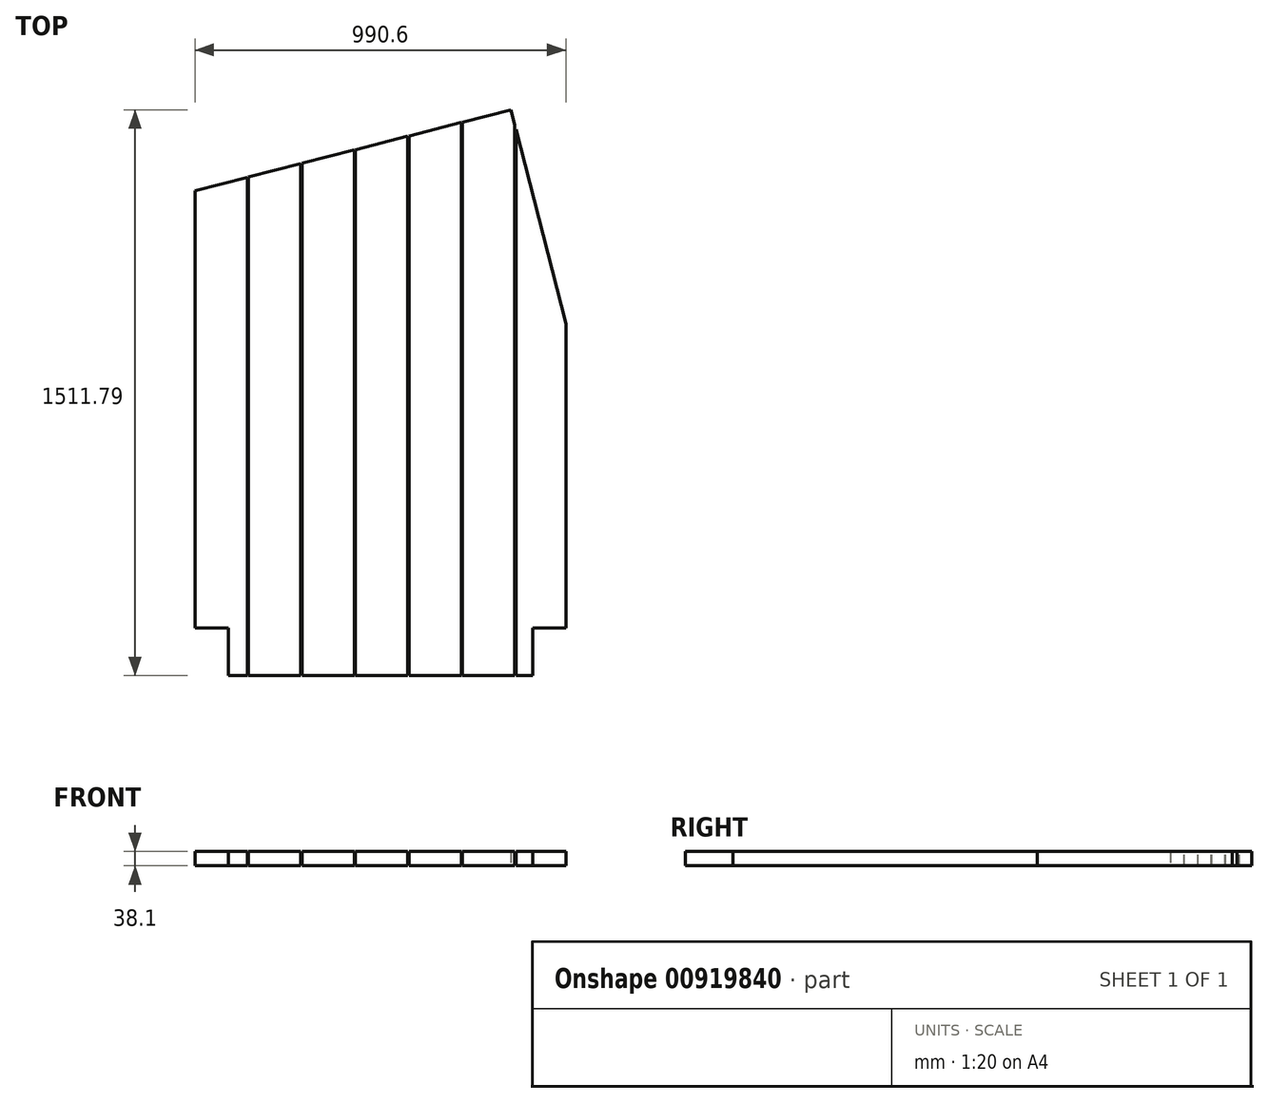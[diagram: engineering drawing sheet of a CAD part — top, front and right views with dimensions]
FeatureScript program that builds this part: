
annotation { "Feature Type Name" : "Feature", "Feature Type Description" : "" }
export const myFeature = defineFeature(function(context is Context, id is Id, definition is map)
    precondition{}
    {
        {
            var Q0;
            Q0=qCreatedBy(makeId("Top.planeOp"),FACE);
            var sketch = newSketch(context, id + "F0", { "sketchPlane" : qUnion([Q0])});
            skLineSegment(sketch, "E0", {"start": v(0, 0) * mm, "end": v(0, 1168.4) * mm});
            skLineSegment(sketch, "E1", {"start": v(0, 1168.4) * mm, "end": v(843.93, 1384.8) * mm});
            skLineSegment(sketch, "E2", {"start": v(843.93, 1384.8) * mm, "end": v(990.6, 812.8) * mm});
            skLineSegment(sketch, "E3", {"start": v(990.6, 812.8) * mm, "end": v(990.6, 0) * mm});
            skLineSegment(sketch, "E4", {"start": v(990.6, 0) * mm, "end": v(0, 0) * mm});
            skSolve(sketch);
        }
        {
            var Q0;
            Q0 = qSketchRegion(id + "F0", true);
            extrude(context, id + "F1", {"entities" : qUnion([Q0]), "depth" : 38.1 * mm, "offsetDistance" : 25.4 * mm});
        }
        {
            var Q0;
            Q0=makeQuery(id+"F1.opExtrude","CAP_FACE",FACE,{"disambiguationData":[OSD([sQuery(id+"F0.wireOp",EDGE,"E0"),sQuery(id+"F0.wireOp",EDGE,"E1"),sQuery(id+"F0.wireOp",EDGE,"E2"),sQuery(id+"F0.wireOp",EDGE,"E3"),sQuery(id+"F0.wireOp",EDGE,"E4")])],"isStart":false});
            var sketch = newSketch(context, id + "F2", { "sketchPlane" : qUnion([Q0])});
            skLineSegment(sketch, "E5.bottom", {"start": v(88.9, 0) * mm, "end": v(901.7, 0) * mm});
            skLineSegment(sketch, "E5.top", {"start": v(88.9, -127) * mm, "end": v(901.7, -127) * mm});
            skLineSegment(sketch, "E5.left", {"start": v(88.9, 0) * mm, "end": v(88.9, -127) * mm});
            skLineSegment(sketch, "E5.right", {"start": v(901.7, 0) * mm, "end": v(901.7, -127) * mm});
            skSolve(sketch);
        }
        {
            var Q0;
            Q0=makeQuery(id+"F2.imprint","IMPRINT",FACE,{"disambiguationData":[TD([[makeQuery(id+"F2.imprint","IMPRINT",EDGE,{"derivedFrom":sQuery(id+"F2.wireOp",EDGE,"E5.bottom")}),1.0]])]});
            extrude(context, id + "F3", {"entities" : qUnion([Q0]), "operationType" : NewBodyOperationType.ADD, "oppositeDirection" : true, "depth" : 38.1 * mm, "offsetDistance" : 25.4 * mm});
        }
        {
            var Q0;
            Q0=makeQuery(id+"F3.boolean.opBoolean","MERGE",FACE,{"derivedFrom":[makeQuery(id+"F1.opExtrude","CAP_FACE",FACE,{"disambiguationData":[OSD([sQuery(id+"F0.wireOp",EDGE,"E0"),sQuery(id+"F0.wireOp",EDGE,"E1"),sQuery(id+"F0.wireOp",EDGE,"E2"),sQuery(id+"F0.wireOp",EDGE,"E3"),sQuery(id+"F0.wireOp",EDGE,"E4")])],"isStart":false}),makeQuery(id+"F3.opExtrude","CAP_FACE",FACE,{"disambiguationData":[OSD([sQuery(id+"F2.wireOp",EDGE,"E5.bottom"),sQuery(id+"F2.wireOp",EDGE,"E5.top"),sQuery(id+"F2.wireOp",EDGE,"E5.left"),sQuery(id+"F2.wireOp",EDGE,"E5.right")])],"isStart":true})]});
            var sketch = newSketch(context, id + "F4", { "sketchPlane" : qUnion([Q0])});
            skLineSegment(sketch, "E6", {"start": v(139.7, -127) * mm, "end": v(139.7, 1204.22) * mm});
            skLineSegment(sketch, "E7", {"start": v(142.87, 1205.03) * mm, "end": v(142.88, -127) * mm});
            skLineSegment(sketch, "E8", {"start": v(282.57, 1240.86) * mm, "end": v(282.58, -127) * mm});
            skLineSegment(sketch, "E9", {"start": v(285.75, 1241.67) * mm, "end": v(285.75, -127) * mm});
            skLineSegment(sketch, "E10", {"start": v(425.45, 1277.49) * mm, "end": v(425.45, -127) * mm});
            skLineSegment(sketch, "E11", {"start": v(428.62, 1278.3) * mm, "end": v(428.63, -127) * mm});
            skLineSegment(sketch, "E12", {"start": v(568.33, -127) * mm, "end": v(568.32, 1314.12) * mm});
            skLineSegment(sketch, "E13", {"start": v(571.5, 1314.94) * mm, "end": v(571.5, -127) * mm});
            skLineSegment(sketch, "E14", {"start": v(711.2, 1902.46) * mm, "end": v(711.2, -127) * mm});
            skLineSegment(sketch, "E15", {"start": v(714.37, 1351.57) * mm, "end": v(714.38, -127) * mm});
            skLineSegment(sketch, "E16", {"start": v(854.08, -127) * mm, "end": v(854.07, 1387.4) * mm});
            skLineSegment(sketch, "E17", {"start": v(857.25, 1332.87) * mm, "end": v(857.25, -127) * mm});
            skLineSegment(sketch, "E18", {"start": v(996.95, 788.03) * mm, "end": v(996.95, 0) * mm});
            skSolve(sketch);
        }
        {
            var Q0;
            {var subQ0=sQuery(id+"F4.wireOp",EDGE,"E6");Q0=makeQuery(id+"F4.imprint","IMPRINT",FACE,{"disambiguationData":[TD([[makeQuery(id+"F4.imprint","IMPRINT",EDGE,{"derivedFrom":subQ0}),-1.0]])]});}
            var Q1;
            {var subQ0=sQuery(id+"F4.wireOp",EDGE,"E8");Q1=makeQuery(id+"F4.imprint","IMPRINT",FACE,{"disambiguationData":[TD([[makeQuery(id+"F4.imprint","IMPRINT",EDGE,{"derivedFrom":subQ0}),1.0]])]});}
            var Q2;
            {var subQ0=sQuery(id+"F4.wireOp",EDGE,"E10");Q2=makeQuery(id+"F4.imprint","IMPRINT",FACE,{"disambiguationData":[TD([[makeQuery(id+"F4.imprint","IMPRINT",EDGE,{"derivedFrom":subQ0}),1.0]])]});}
            var Q3;
            {var subQ0=sQuery(id+"F4.wireOp",EDGE,"E12");Q3=makeQuery(id+"F4.imprint","IMPRINT",FACE,{"disambiguationData":[TD([[makeQuery(id+"F4.imprint","IMPRINT",EDGE,{"derivedFrom":subQ0}),-1.0]])]});}
            var Q4;
            {var subQ5=sQuery(id+"F4.wireOp",EDGE,"E15");Q4=makeQuery(id+"F4.imprint","IMPRINT",FACE,{"disambiguationData":[TD([[makeQuery(id+"F4.imprint","IMPRINT",EDGE,{"derivedFrom":subQ5}),-1.0]])]});}
            var Q5;
            {var subQ5=sQuery(id+"F4.wireOp",EDGE,"E17");Q5=makeQuery(id+"F4.imprint","IMPRINT",FACE,{"disambiguationData":[TD([[makeQuery(id+"F4.imprint","IMPRINT",EDGE,{"derivedFrom":subQ5}),-1.0]])]});}
            extrude(context, id + "F5", {"entities" : qUnion([Q0, Q1, Q2, Q3, Q4, Q5]), "operationType" : NewBodyOperationType.REMOVE, "endBound" : BoundingType.THROUGH_ALL, "oppositeDirection" : true, "depth" : 25.4 * mm, "offsetDistance" : 25.4 * mm});
        }
    });
